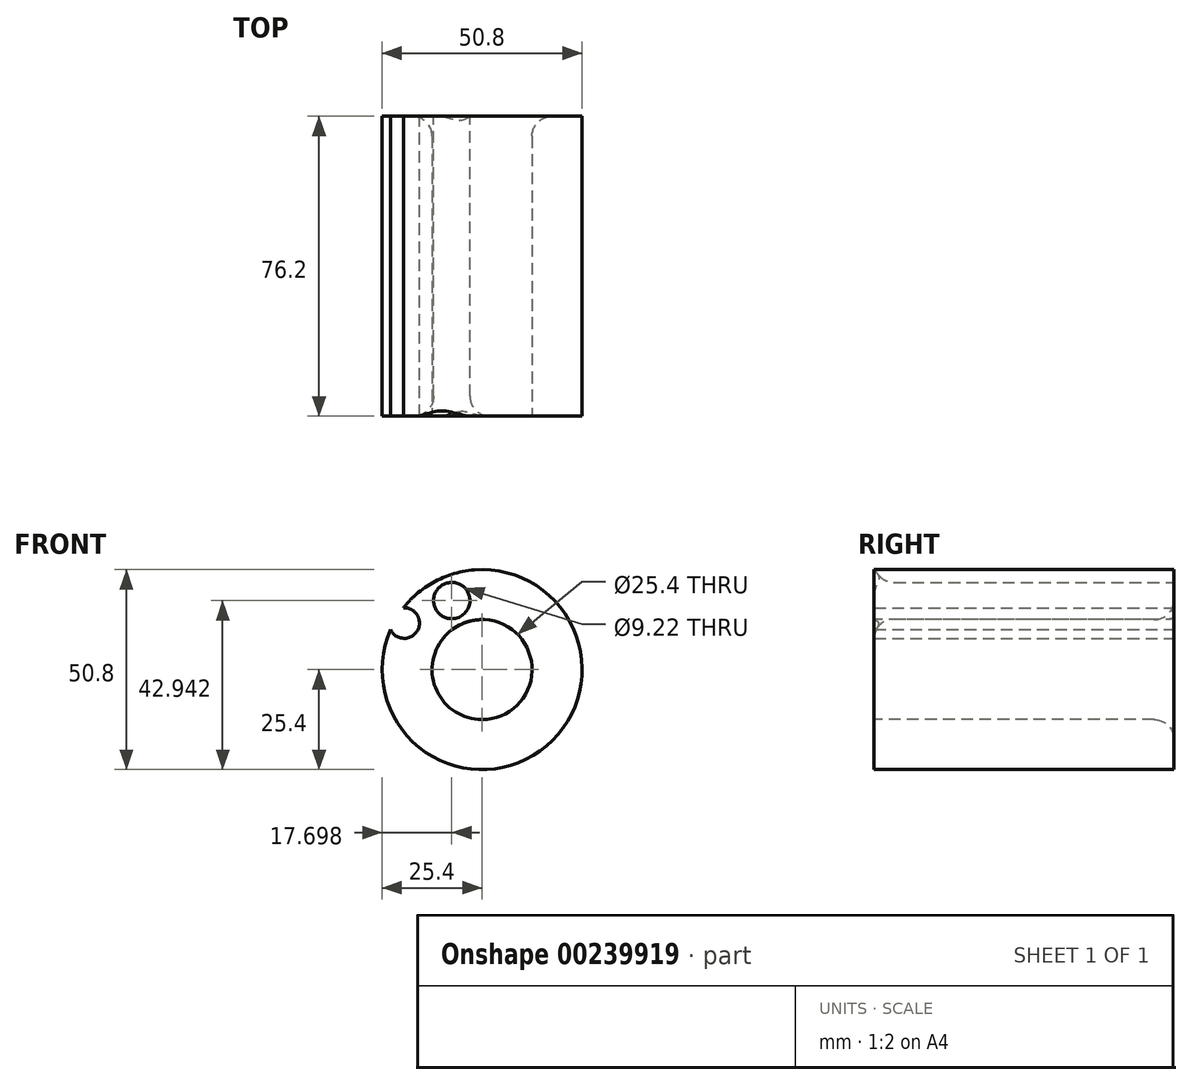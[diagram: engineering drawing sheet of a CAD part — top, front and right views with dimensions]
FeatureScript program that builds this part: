
annotation { "Feature Type Name" : "Feature", "Feature Type Description" : "" }
export const myFeature = defineFeature(function(context is Context, id is Id, definition is map)
    precondition{}
    {
        {
            var Q0;
            Q0=qCreatedBy(makeId("Front.planeOp"),FACE);
            var sketch = newSketch(context, id + "F0", { "sketchPlane" : qUnion([Q0])});
            skCircle(sketch, "E0", {"center": v(0, 0) * mm, "radius": 25.4 * mm});
            skSolve(sketch);
        }
        {
            var Q0;
            Q0 = qSketchRegion(id + "F0", true);
            extrude(context, id + "F1", {"entities" : qUnion([Q0]), "depth" : 76.2 * mm});
        }
        {
            var Q0;
            Q0=makeQuery(id+"F1.opExtrude","CAP_FACE",FACE,{"disambiguationData":[OSD([sQuery(id+"F0.wireOp",EDGE,"E0")])],"isStart":false});
            var sketch = newSketch(context, id + "F2", { "sketchPlane" : qUnion([Q0])});
            skCircle(sketch, "E1", {"center": v(0, 0) * mm, "radius": 12.7 * mm});
            skSolve(sketch);
        }
        {
            var Q0;
            Q0 = qSketchRegion(id + "F2", true);
            extrude(context, id + "F3", {"entities" : qUnion([Q0]), "operationType" : NewBodyOperationType.REMOVE, "oppositeDirection" : true, "depth" : 105.4 * mm});
        }
        {
            var Q0;
            Q0=qCreatedBy(makeId("Front.planeOp"),FACE);
            var sketch = newSketch(context, id + "F4", { "sketchPlane" : qUnion([Q0])});
            skCircle(sketch, "E2", {"center": v(-19.78, 11.83) * mm, "radius": 3.88 * mm});
            skSolve(sketch);
        }
        {
            var Q0;
            Q0 = qSketchRegion(id + "F4", true);
            extrude(context, id + "F5", {"entities" : qUnion([Q0]), "operationType" : NewBodyOperationType.REMOVE, "depth" : 133.35 * mm});
        }
        {
            var Q0;
            Q0=qCreatedBy(makeId("Front.planeOp"),FACE);
            var sketch = newSketch(context, id + "F6", { "sketchPlane" : qUnion([Q0])});
            skCircle(sketch, "E3", {"center": v(-7.7, 17.54) * mm, "radius": 4.6 * mm});
            skSolve(sketch);
        }
        {
            var Q0;
            Q0 = qSketchRegion(id + "F6", true);
            extrude(context, id + "F7", {"entities" : qUnion([Q0]), "operationType" : NewBodyOperationType.REMOVE, "depth" : 145.54 * mm});
        }
        {
            var Q0;
            Q0=makeQuery(id+"F3.boolean.opBoolean","COPY",EDGE,{"derivedFrom":makeQuery(id+"F3.opExtrude","CAP_EDGE",EDGE,{"disambiguationData":[OSD([sQuery(id+"F2.wireOp",EDGE,"E1")])],"isStart":true})});
            var Q1;
            Q1=makeQuery(id+"F7.boolean.opBoolean","INTERSECT",EDGE,{"derivedFrom":[makeQuery(id+"F1.opExtrude","CAP_FACE",FACE,{"disambiguationData":[OSD([sQuery(id+"F0.wireOp",EDGE,"E0")])],"isStart":false}),makeQuery(id+"F7.opExtrude","SWEPT_FACE",FACE,{"disambiguationData":[OSD([sQuery(id+"F6.wireOp",EDGE,"E3")])]})]});
            fillet(context, id + "F8", {"entities" : qUnion([Q0, Q1]), "radius" : 5.08 * mm, "tangentPropagation" : true, "allowEdgeOverflow" : false});
        }
        {
            var Q0;
            Q0=makeQuery(id+"F3.boolean.opBoolean","INTERSECT",EDGE,{"derivedFrom":[makeQuery(id+"F1.opExtrude","CAP_FACE",FACE,{"disambiguationData":[OSD([sQuery(id+"F0.wireOp",EDGE,"E0")])],"isStart":true}),makeQuery(id+"F3.opExtrude","SWEPT_FACE",FACE,{"disambiguationData":[OSD([sQuery(id+"F2.wireOp",EDGE,"E1")])]})]});
            var Q1;
            Q1=makeQuery(id+"F7.boolean.opBoolean","COPY",EDGE,{"derivedFrom":makeQuery(id+"F7.opExtrude","CAP_EDGE",EDGE,{"disambiguationData":[OSD([sQuery(id+"F6.wireOp",EDGE,"E3")])],"isStart":true})});
            fillet(context, id + "F9", {"entities" : qUnion([Q0, Q1]), "radius" : 5.08 * mm, "tangentPropagation" : true, "allowEdgeOverflow" : false});
        }
    });
